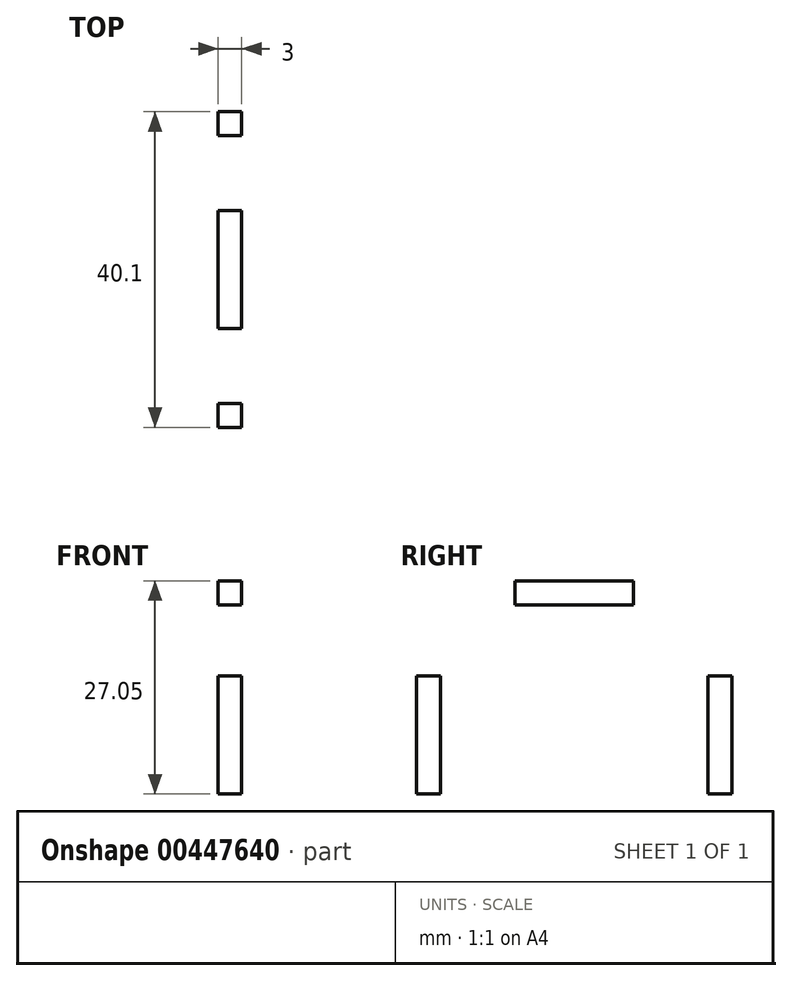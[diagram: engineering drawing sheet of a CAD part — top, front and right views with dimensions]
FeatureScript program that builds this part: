
annotation { "Feature Type Name" : "Feature", "Feature Type Description" : "" }
export const myFeature = defineFeature(function(context is Context, id is Id, definition is map)
    precondition{}
    {
        {
            var Q0;
            Q0=qCreatedBy(makeId("Right.planeOp"),FACE);
            var sketch = newSketch(context, id + "F0", { "sketchPlane" : qUnion([Q0])});
            skLineSegment(sketch, "E0.bottom", {"start": v(17, 16.5) * mm, "end": v(-17, 16.5) * mm});
            skLineSegment(sketch, "E0.top", {"start": v(17, -16.5) * mm, "end": v(-17, -16.5) * mm});
            skLineSegment(sketch, "E0.left", {"start": v(17, 16.5) * mm, "end": v(17, -16.5) * mm});
            skLineSegment(sketch, "E0.right", {"start": v(-17, 16.5) * mm, "end": v(-17, -16.5) * mm});
            skPoint(sketch, "E0.middle", {"position": v(0, 0) * mm});
            skLineSegment(sketch, "E1.bottom", {"start": v(7.5, 19.55) * mm, "end": v(-7.5, 19.55) * mm});
            skLineSegment(sketch, "E1.top", {"start": v(7.5, 16.5) * mm, "end": v(-7.5, 16.5) * mm});
            skLineSegment(sketch, "E1.left", {"start": v(7.5, 19.55) * mm, "end": v(7.5, 16.5) * mm});
            skLineSegment(sketch, "E1.right", {"start": v(-7.5, 19.55) * mm, "end": v(-7.5, 16.5) * mm});
            skPoint(sketch, "E1.middle", {"position": v(0, 18.02) * mm});
            skLineSegment(sketch, "E2.bottom", {"start": v(4.95, 3.5) * mm, "end": v(-4.95, 3.5) * mm});
            skLineSegment(sketch, "E2.top", {"start": v(4.95, 6.5) * mm, "end": v(-4.95, 6.5) * mm});
            skLineSegment(sketch, "E2.left", {"start": v(4.95, 3.5) * mm, "end": v(4.95, 6.5) * mm});
            skLineSegment(sketch, "E2.right", {"start": v(-4.95, 3.5) * mm, "end": v(-4.95, 6.5) * mm});
            skLineSegment(sketch, "E3.top", {"start": v(7.45, -13.45) * mm, "end": v(-7.45, -13.45) * mm});
            skLineSegment(sketch, "E3.left", {"start": v(7.45, -16.5) * mm, "end": v(7.45, -13.45) * mm});
            skLineSegment(sketch, "E3.right", {"start": v(-7.45, -16.5) * mm, "end": v(-7.45, -13.45) * mm});
            skPoint(sketch, "E3.middle", {"position": v(0, -14.97) * mm});
            skLineSegment(sketch, "E4.bottom", {"start": v(-20.05, -7.5) * mm, "end": v(-17, -7.5) * mm});
            skLineSegment(sketch, "E4.top", {"start": v(-20.05, 7.5) * mm, "end": v(-17, 7.5) * mm});
            skLineSegment(sketch, "E4.left", {"start": v(-20.05, -7.5) * mm, "end": v(-20.05, 7.5) * mm});
            skLineSegment(sketch, "E4.right", {"start": v(-17, -7.5) * mm, "end": v(-17, 7.5) * mm});
            skPoint(sketch, "E4.middle", {"position": v(-18.52, 0) * mm});
            skLineSegment(sketch, "E5.bottom", {"start": v(20.05, -7.5) * mm, "end": v(17, -7.5) * mm});
            skLineSegment(sketch, "E5.top", {"start": v(20.05, 7.5) * mm, "end": v(17, 7.5) * mm});
            skLineSegment(sketch, "E5.left", {"start": v(20.05, -7.5) * mm, "end": v(20.05, 7.5) * mm});
            skLineSegment(sketch, "E5.right", {"start": v(17, -7.5) * mm, "end": v(17, 7.5) * mm});
            skPoint(sketch, "E5.middle", {"position": v(18.52, 0) * mm});
            skLineSegment(sketch, "E6.bottom", {"start": v(9.5, -11.97) * mm, "end": v(-9.5, -11.97) * mm});
            skLineSegment(sketch, "E6.top", {"start": v(9.5, 0.03) * mm, "end": v(-9.5, 0.03) * mm});
            skLineSegment(sketch, "E6.left", {"start": v(9.5, -11.97) * mm, "end": v(9.5, 0.03) * mm});
            skLineSegment(sketch, "E6.right", {"start": v(-9.5, -11.97) * mm, "end": v(-9.5, 0.03) * mm});
            skPoint(sketch, "E6.middle", {"position": v(0, -5.97) * mm});
            skSolve(sketch);
        }
        {
            var Q0;
            {var subQ0=sQuery(id+"F0.wireOp",EDGE,"E1.top");Q0=makeQuery(id+"F0.imprint","IMPRINT",FACE,{"disambiguationData":[TD([[makeQuery(id+"F0.imprint","IMPRINT",EDGE,{"derivedFrom":subQ0}),1.0]])]});}
            var Q1;
            Q1=makeQuery(id+"F0.imprint","IMPRINT",FACE,{"disambiguationData":[TD([[makeQuery(id+"F0.imprint","IMPRINT",EDGE,{"derivedFrom":sQuery(id+"F0.wireOp",EDGE,"E1.bottom")}),1.0]])]});
            var Q2;
            Q2=makeQuery(id+"F0.imprint","IMPRINT",FACE,{"disambiguationData":[TD([[makeQuery(id+"F0.imprint","IMPRINT",EDGE,{"derivedFrom":sQuery(id+"F0.wireOp",EDGE,"E4.bottom")}),1.0]])]});
            var Q3;
            Q3=makeQuery(id+"F0.imprint","IMPRINT",FACE,{"disambiguationData":[TD([[makeQuery(id+"F0.imprint","IMPRINT",EDGE,{"derivedFrom":sQuery(id+"F0.wireOp",EDGE,"E5.bottom")}),-1.0]])]});
            extrude(context, id + "F1", {"entities" : qUnion([Q0, Q1, Q2, Q3]), "depth" : 3 * mm});
        }
    });
